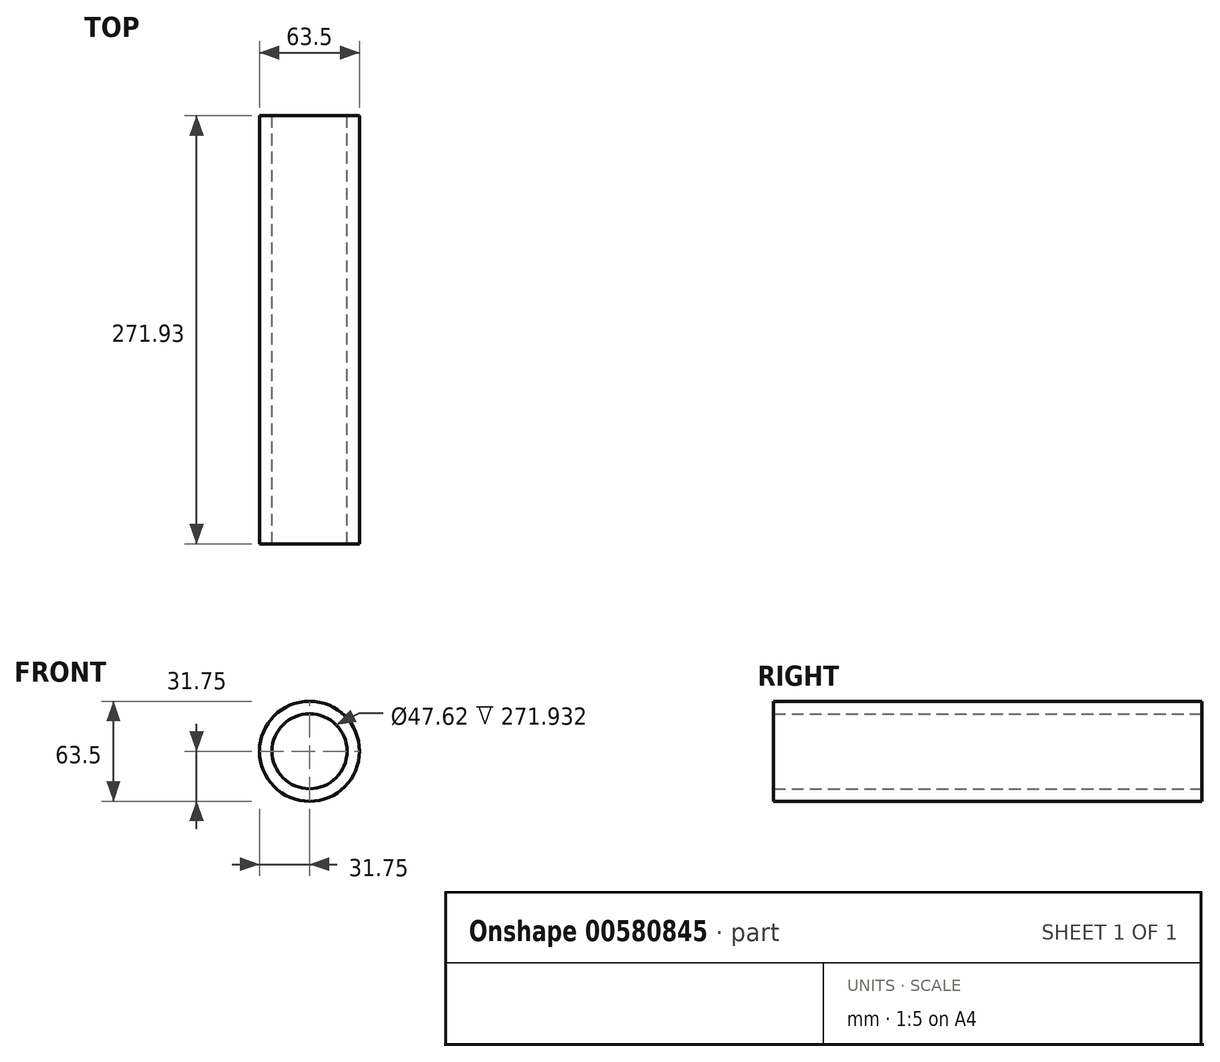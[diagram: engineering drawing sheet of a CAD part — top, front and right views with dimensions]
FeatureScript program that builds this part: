
annotation { "Feature Type Name" : "Feature", "Feature Type Description" : "" }
export const myFeature = defineFeature(function(context is Context, id is Id, definition is map)
    precondition{}
    {
        {
            var Q0;
            Q0=qCreatedBy(makeId("Front.planeOp"),FACE);
            var sketch = newSketch(context, id + "F0", { "sketchPlane" : qUnion([Q0])});
            skCircle(sketch, "E0", {"center": v(0, 0) * mm, "radius": 31.75 * mm});
            skCircle(sketch, "E1", {"center": v(0, 0) * mm, "radius": 23.81 * mm});
            skSolve(sketch);
        }
        {
            var Q0;
            Q0=makeQuery(id+"F0.imprint","IMPRINT",FACE,{"disambiguationData":[TD([[makeQuery(id+"F0.imprint","IMPRINT",EDGE,{"derivedFrom":sQuery(id+"F0.wireOp",EDGE,"E0")}),1.0]])]});
            extrude(context, id + "F1", {"entities" : qUnion([Q0]), "depth" : 271.93 * mm, "offsetDistance" : 25.4 * mm});
        }
    });
